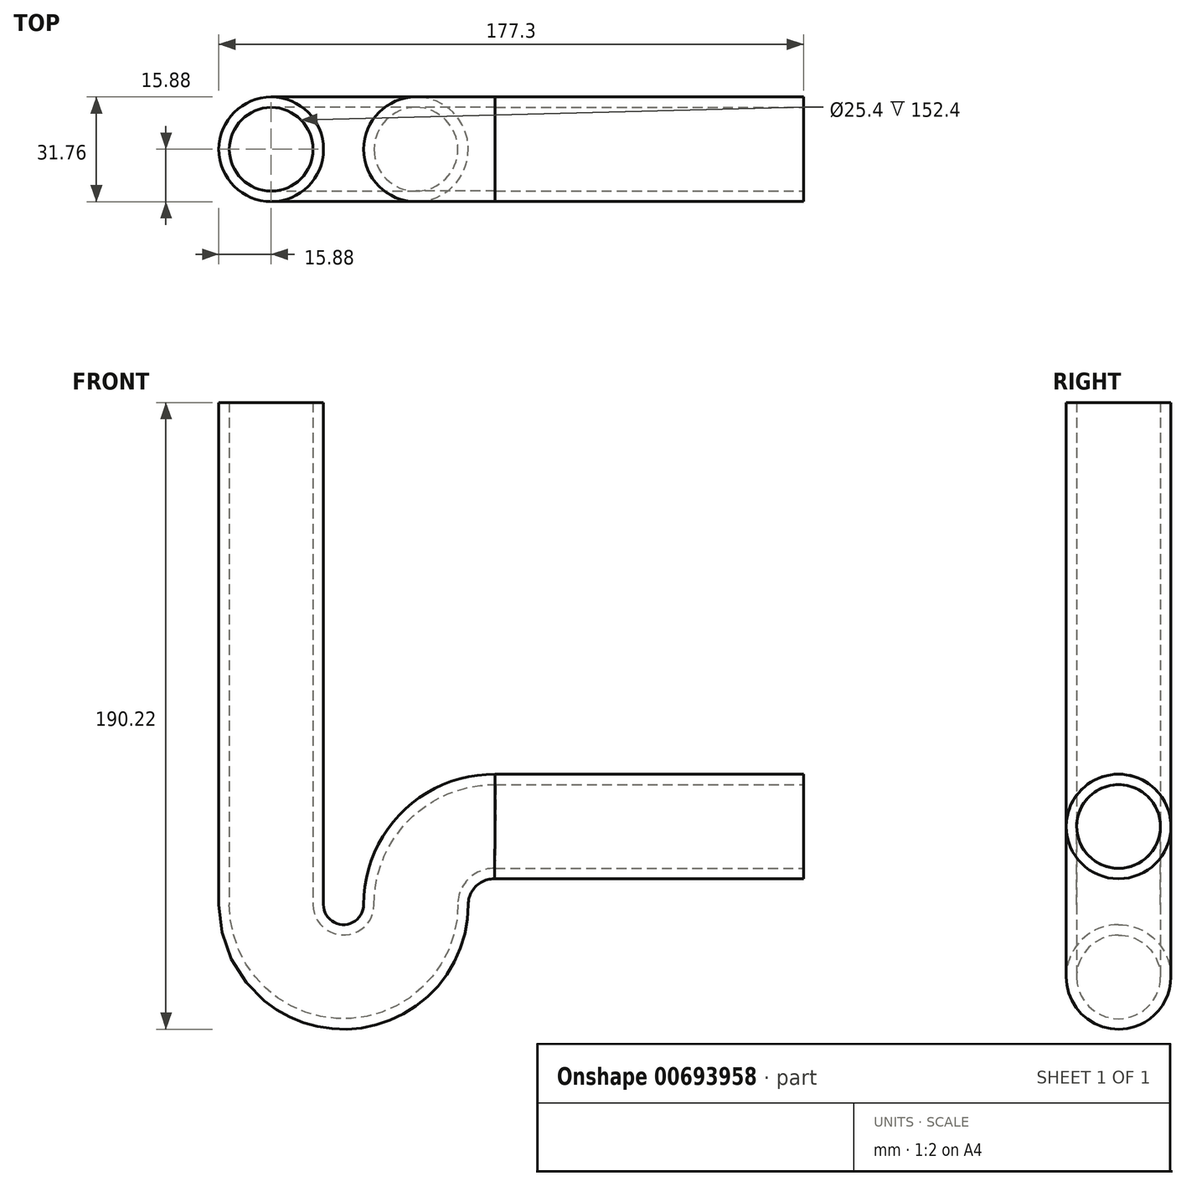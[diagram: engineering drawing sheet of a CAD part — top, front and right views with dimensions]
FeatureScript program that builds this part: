
annotation { "Feature Type Name" : "Feature", "Feature Type Description" : "" }
export const myFeature = defineFeature(function(context is Context, id is Id, definition is map)
    precondition{}
    {
        {
            var Q0;
            Q0=qCreatedBy(makeId("Top.planeOp"),FACE);
            var sketch = newSketch(context, id + "F0", { "sketchPlane" : qUnion([Q0])});
            skCircle(sketch, "E0", {"center": v(0, 0) * mm, "radius": 12.7 * mm});
            skCircle(sketch, "E1", {"center": v(0, 0) * mm, "radius": 15.88 * mm});
            skSolve(sketch);
        }
        {
            var Q0;
            Q0=qCreatedBy(makeId("Front.planeOp"),FACE);
            var sketch = newSketch(context, id + "F1", { "sketchPlane" : qUnion([Q0])});
            skLineSegment(sketch, "E2", {"start": v(0, 0) * mm, "end": v(0, -152.4) * mm});
            skArc(sketch, "E3", {"start": v(0, -152.4) * mm, "mid": v(21.95, -174.35) * mm, "end": v(43.9, -152.4) * mm});
            skArc(sketch, "E4", {"start": v(43.9, -152.4) * mm, "mid": v(50.93, -135.55) * mm, "end": v(67.85, -128.68) * mm});
            skLineSegment(sketch, "E5", {"start": v(67.85, -128.68) * mm, "end": v(161.42, -128.68) * mm});
            skSolve(sketch);
        }
        {
            var Q0;
            Q0=makeQuery(id+"F0.imprint","IMPRINT",FACE,{"disambiguationData":[TD([[makeQuery(id+"F0.imprint","IMPRINT",EDGE,{"derivedFrom":sQuery(id+"F0.wireOp",EDGE,"E0")}),-1.0]])]});
            var Q1;
            Q1=sQuery(id+"F1.wireOp",EDGE,"E2");
            var Q2;
            Q2=sQuery(id+"F1.wireOp",EDGE,"E3");
            var Q3;
            Q3=sQuery(id+"F1.wireOp",EDGE,"E4");
            var Q4;
            Q4=sQuery(id+"F1.wireOp",EDGE,"E5");
            sweep(context, id + "F2", {"profiles" : qUnion([Q0]), "path" : qUnion([Q1, Q2, Q3, Q4])});
        }
    });
